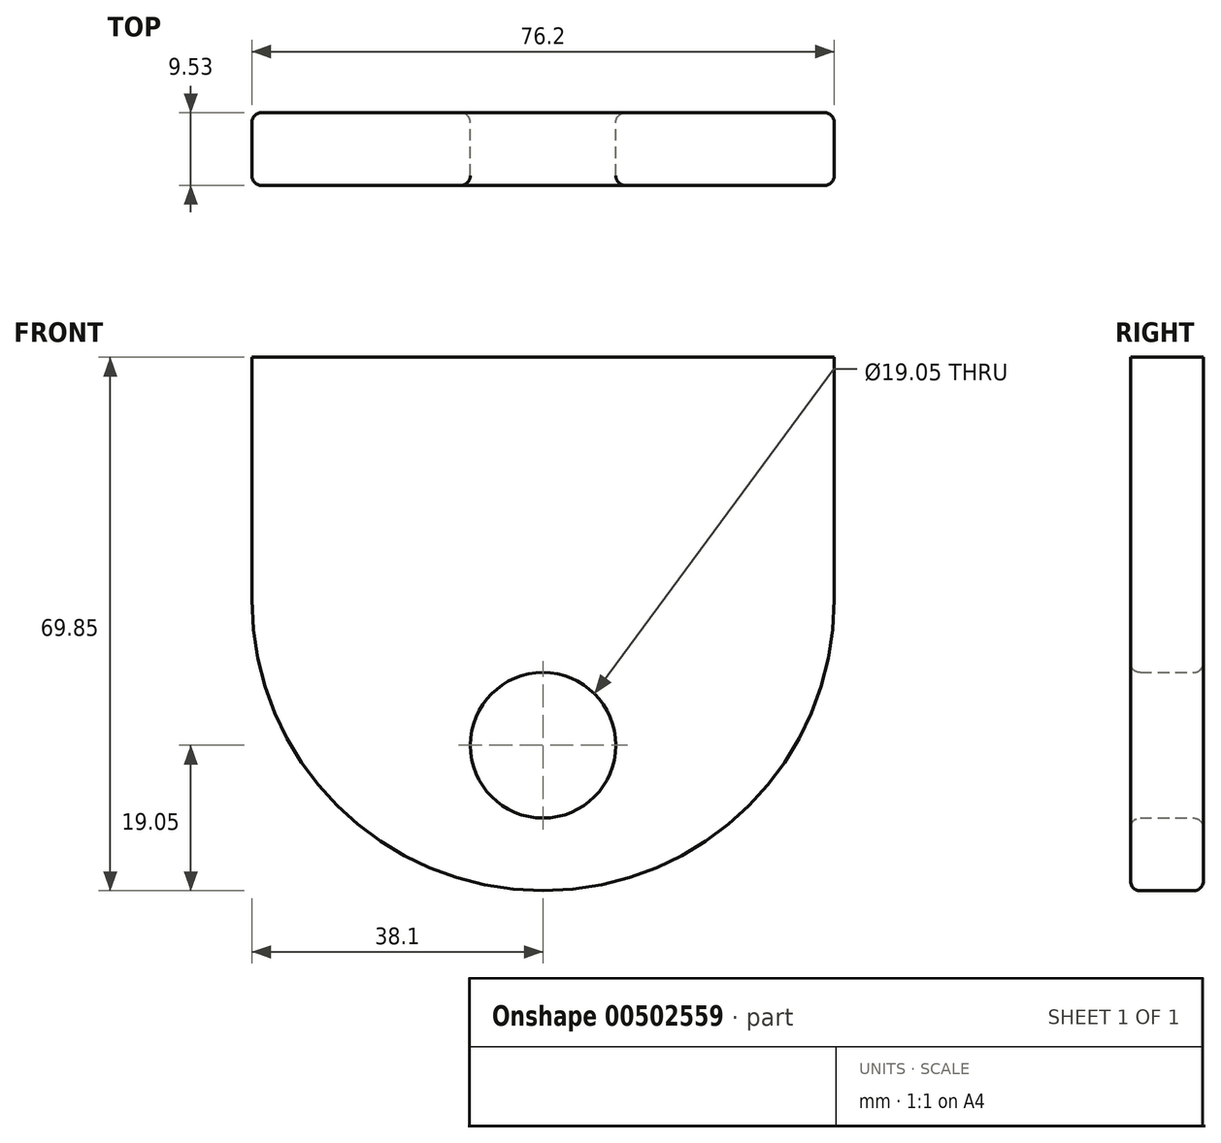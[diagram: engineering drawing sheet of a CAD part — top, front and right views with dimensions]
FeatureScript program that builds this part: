
annotation { "Feature Type Name" : "Feature", "Feature Type Description" : "" }
export const myFeature = defineFeature(function(context is Context, id is Id, definition is map)
    precondition{}
    {
        {
            var Q0;
            Q0=qCreatedBy(makeId("Front.planeOp"),FACE);
            var sketch = newSketch(context, id + "F0", { "sketchPlane" : qUnion([Q0])});
            skArc(sketch, "E0", {"start": v(-38.1, 0) * mm, "mid": v(0, -38.1) * mm, "end": v(38.1, 0) * mm});
            skLineSegment(sketch, "E1", {"start": v(0, 0) * mm, "end": v(38.1, 0) * mm});
            skLineSegment(sketch, "E2", {"start": v(38.1, 0) * mm, "end": v(-38.1, 0) * mm});
            skLineSegment(sketch, "E3", {"start": v(-38.1, 0) * mm, "end": v(-38.1, 31.75) * mm});
            skLineSegment(sketch, "E4", {"start": v(-38.1, 31.75) * mm, "end": v(38.1, 31.75) * mm});
            skLineSegment(sketch, "E5", {"start": v(38.1, 31.75) * mm, "end": v(38.1, 0) * mm});
            skLineSegment(sketch, "E6", {"start": v(0, 0) * mm, "end": v(0, -19.05) * mm});
            skCircle(sketch, "E7", {"center": v(0, -19.05) * mm, "radius": 9.53 * mm});
            skSolve(sketch);
        }
        {
            var Q0;
            {var subQ0=sQuery(id+"F0.wireOp",EDGE,"E3");Q0=makeQuery(id+"F0.imprint","IMPRINT",FACE,{"disambiguationData":[TD([[makeQuery(id+"F0.imprint","IMPRINT",EDGE,{"derivedFrom":subQ0}),-1.0]])]});}
            var Q1;
            {var subQ0=sQuery(id+"F0.wireOp",EDGE,"E0");Q1=makeQuery(id+"F0.imprint","IMPRINT",FACE,{"disambiguationData":[TD([[makeQuery(id+"F0.imprint","IMPRINT",EDGE,{"derivedFrom":subQ0}),1.0]])]});}
            extrude(context, id + "F1", {"entities" : qUnion([Q0, Q1]), "depth" : 9.52 * mm});
        }
        {
            var Q0;
            Q0=makeQuery(id+"F1.opExtrude","CAP_EDGE",EDGE,{"disambiguationData":[OSD([sQuery(id+"F0.wireOp",EDGE,"E3")])],"isStart":false});
            var Q1;
            Q1=makeQuery(id+"F1.opExtrude","CAP_EDGE",EDGE,{"disambiguationData":[OSD([sQuery(id+"F0.wireOp",EDGE,"E5")])],"isStart":true});
            var Q2;
            Q2=makeQuery(id+"F1.opExtrude","CAP_EDGE",EDGE,{"disambiguationData":[OSD([sQuery(id+"F0.wireOp",EDGE,"E7")])],"isStart":false});
            var Q3;
            Q3=makeQuery(id+"F1.opExtrude","CAP_EDGE",EDGE,{"disambiguationData":[OSD([sQuery(id+"F0.wireOp",EDGE,"E7")])],"isStart":true});
            fillet(context, id + "F2", {"entities" : qUnion([Q0, Q1, Q2, Q3]), "radius" : 1.27 * mm, "tangentPropagation" : true, "allowEdgeOverflow" : false});
        }
    });
